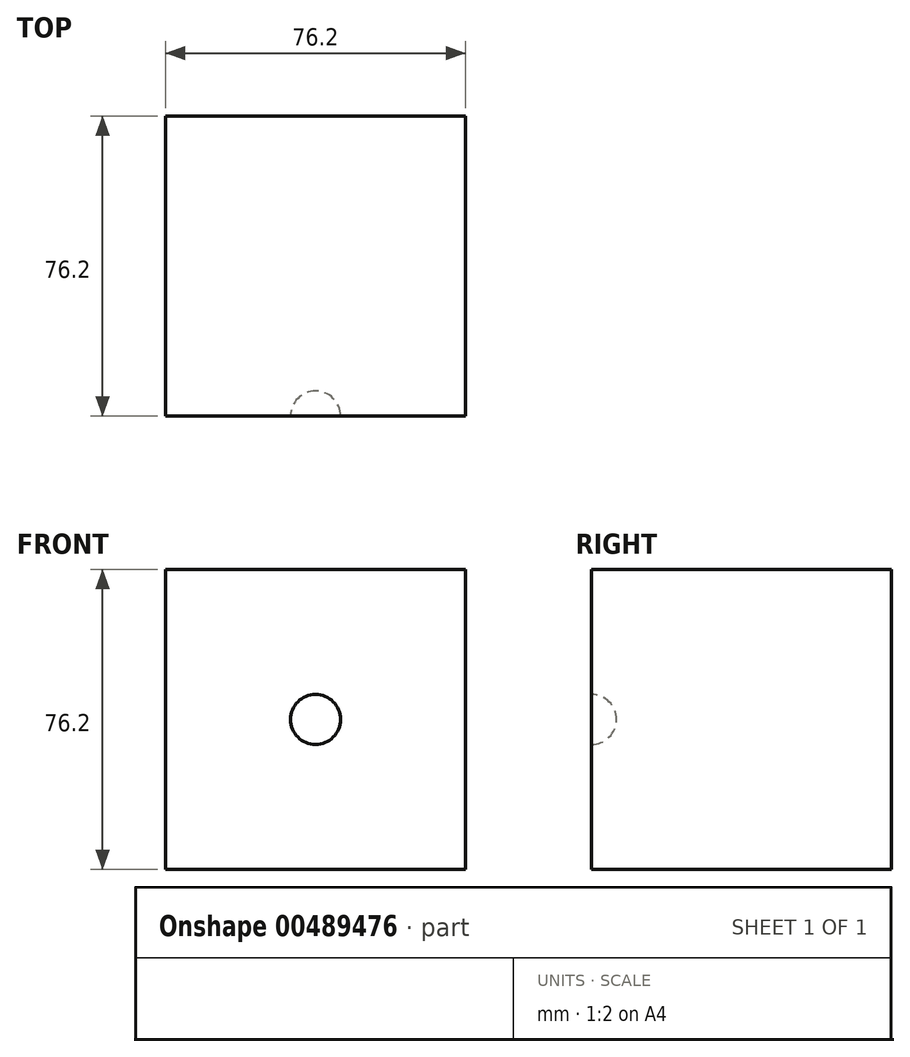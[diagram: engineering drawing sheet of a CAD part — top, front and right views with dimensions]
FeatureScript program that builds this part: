
annotation { "Feature Type Name" : "Feature", "Feature Type Description" : "" }
export const myFeature = defineFeature(function(context is Context, id is Id, definition is map)
    precondition{}
    {
        {
            var Q0;
            Q0=qCreatedBy(makeId("Front.planeOp"),FACE);
            cPlane(context, id + "F0", {"entities" : qUnion([Q0]), "cplaneType" : CPlaneType.OFFSET, "offset" : 76.2 * mm, "width" : 152.4 * mm, "height" : 152.4 * mm});
        }
        {
            var Q0;
            Q0=qCreatedBy(id+"F0.planeOp",FACE);
            var sketch = newSketch(context, id + "F1", { "sketchPlane" : qUnion([Q0])});
            skLineSegment(sketch, "E0", {"start": v(0, 76.2) * mm, "end": v(0, 0) * mm});
            skLineSegment(sketch, "E1", {"start": v(0, 0) * mm, "end": v(76.2, 0) * mm});
            skLineSegment(sketch, "E2", {"start": v(76.2, 0) * mm, "end": v(76.2, 76.2) * mm});
            skLineSegment(sketch, "E3", {"start": v(76.2, 76.2) * mm, "end": v(0, 76.2) * mm});
            skSolve(sketch);
        }
        {
            var Q0;
            Q0 = qSketchRegion(id + "F1", true);
            extrude(context, id + "F2", {"entities" : qUnion([Q0]), "depth" : 76.2 * mm, "offsetDistance" : 25.4 * mm});
        }
        {
            var Q0;
            Q0=makeQuery(id+"F2.opExtrude","CAP_FACE",FACE,{"disambiguationData":[OSD([sQuery(id+"F1.wireOp",EDGE,"E0"),sQuery(id+"F1.wireOp",EDGE,"E1"),sQuery(id+"F1.wireOp",EDGE,"E2"),sQuery(id+"F1.wireOp",EDGE,"E3")])],"isStart":false});
            var sketch = newSketch(context, id + "F3", { "sketchPlane" : qUnion([Q0])});
            skLineSegment(sketch, "E4", {"start": v(38.1, 76.2) * mm, "end": v(38.1, 0) * mm});
            skArc(sketch, "E5", {"start": v(38.1, 31.75) * mm, "mid": v(44.45, 38.1) * mm, "end": v(38.1, 44.45) * mm});
            skPoint(sketch, "E6.orphan", {"position": v(0, 38.1) * mm});
            skPoint(sketch, "E7.orphan", {"position": v(76.2, 38.1) * mm});
            skSolve(sketch);
        }
        {
            var Q0;
            {var subQ0=sQuery(id+"F3.wireOp",EDGE,"E5");Q0=makeQuery(id+"F3.imprint","IMPRINT",FACE,{"disambiguationData":[TD([[makeQuery(id+"F3.imprint","IMPRINT",EDGE,{"derivedFrom":subQ0}),1.0]])]});}
            var Q1;
            Q1=sQuery(id+"F3.wireOp",EDGE,"E4");
            revolve(context, id + "F4", {"operationType" : NewBodyOperationType.REMOVE, "entities" : qUnion([Q0]), "axis" : qUnion([Q1]), "revolveType" : RevolveType.FULL, "oppositeDirection" : true});
        }
    });
